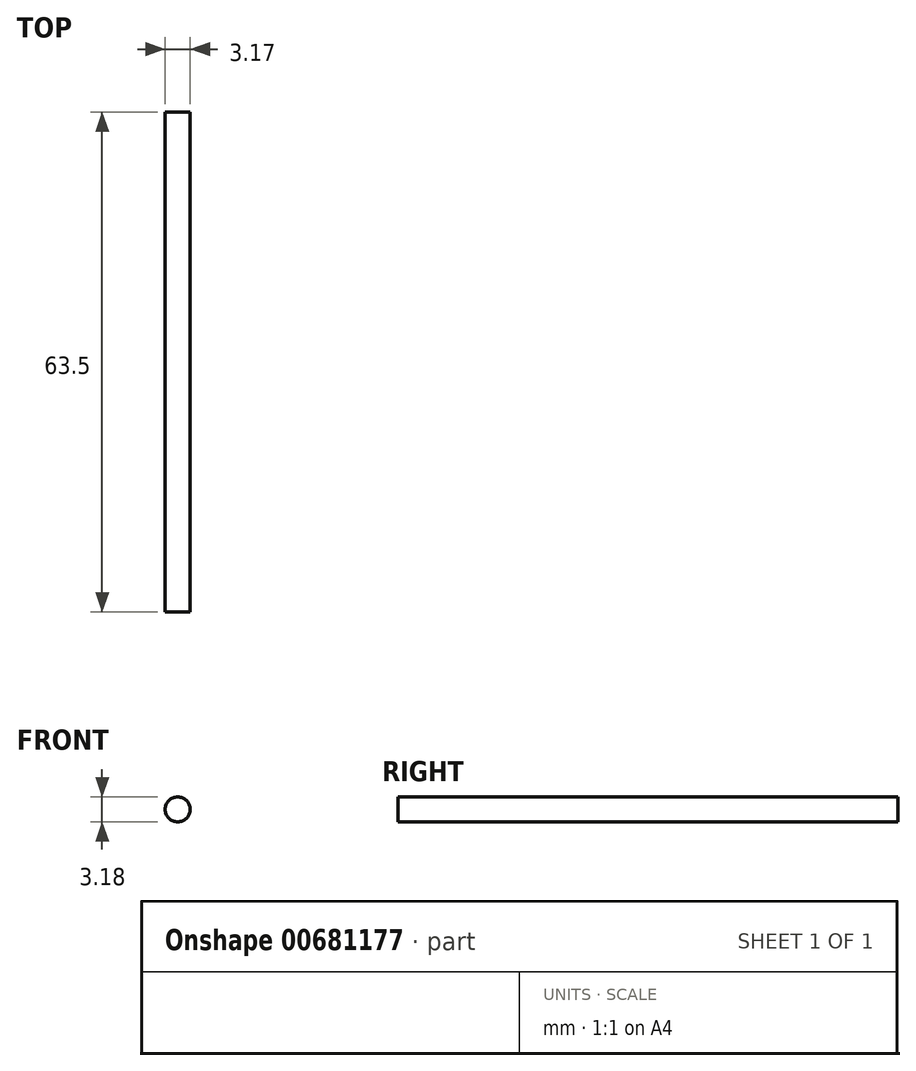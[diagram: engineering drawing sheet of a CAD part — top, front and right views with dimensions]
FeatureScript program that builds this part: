
annotation { "Feature Type Name" : "Feature", "Feature Type Description" : "" }
export const myFeature = defineFeature(function(context is Context, id is Id, definition is map)
    precondition{}
    {
        {
            var Q0;
            Q0=qCreatedBy(makeId("Front.planeOp"),FACE);
            var sketch = newSketch(context, id + "F0", { "sketchPlane" : qUnion([Q0])});
            skCircle(sketch, "E0", {"center": v(-53.98, 13.08) * mm, "radius": 1.59 * mm});
            skSolve(sketch);
        }
        {
            var Q0;
            Q0 = qSketchRegion(id + "F0", true);
            extrude(context, id + "F1", {"entities" : qUnion([Q0]), "depth" : 63.5 * mm, "offsetDistance" : 25.4 * mm});
        }
    });
